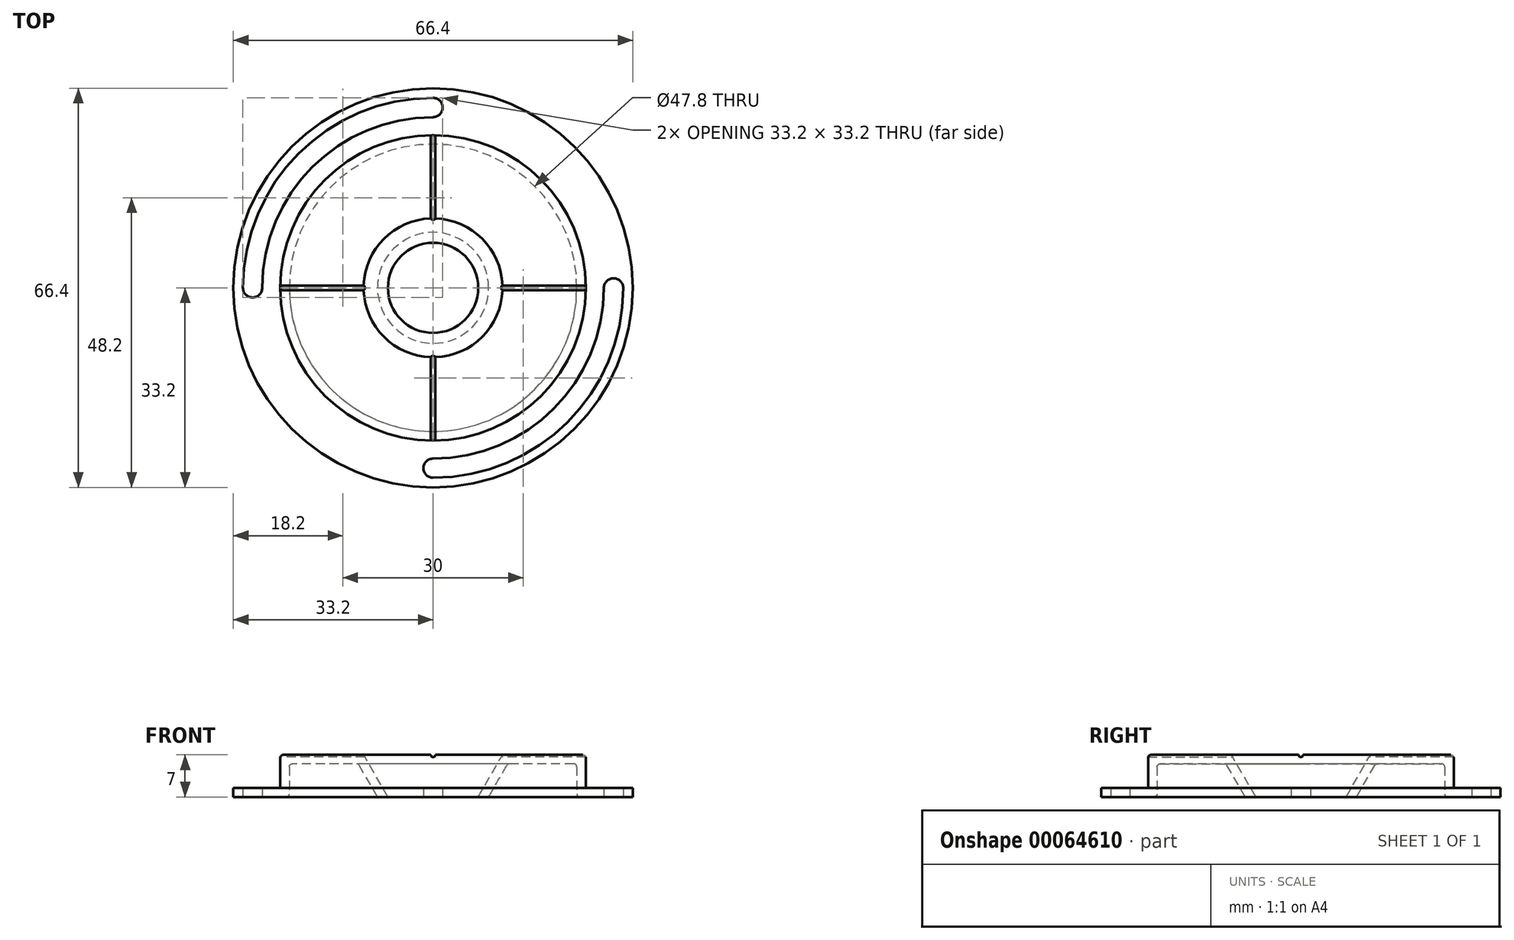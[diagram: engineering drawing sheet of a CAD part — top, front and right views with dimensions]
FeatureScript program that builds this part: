
annotation { "Feature Type Name" : "Feature", "Feature Type Description" : "" }
export const myFeature = defineFeature(function(context is Context, id is Id, definition is map)
    precondition{}
    {
        {
            assignVariable(context, id + "F0", {"name" : "h", "anyValue" : 7});
        }
        {
            assignVariable(context, id + "F1", {"name" : "thickness", "anyValue" : 1.5});
        }
        {
            var Q0;
            Q0=qCreatedBy(makeId("Top.planeOp"),FACE);
            var sketch = newSketch(context, id + "F2", { "sketchPlane" : qUnion([Q0])});
            skLineSegment(sketch, "E0", {"start": v(0, 30) * mm, "end": v(0, -30) * mm, "construction": true});
            skLineSegment(sketch, "E1", {"start": v(-30, 0) * mm, "end": v(30, 0) * mm, "construction": true});
            skLineSegment(sketch, "E2", {"start": v(-21.21, -21.21) * mm, "end": v(21.21, 21.21) * mm, "construction": true});
            skArc(sketch, "E3", {"start": v(-30, 0) * mm, "mid": v(-21.21, -21.21) * mm, "end": v(0, -30) * mm, "construction": true});
            skArc(sketch, "E4", {"start": v(0, -30) * mm, "mid": v(30, 0) * mm, "end": v(0, 30) * mm, "construction": true});
            skArc(sketch, "E5", {"start": v(0, 30) * mm, "mid": v(-21.21, 21.21) * mm, "end": v(-30, 0) * mm, "construction": true});
            skArc(sketch, "E6.0", {"start": v(-22.34, 22.34) * mm, "mid": v(-29.2, 12.1) * mm, "end": v(-31.6, 0) * mm});
            skArc(sketch, "E7.0", {"start": v(-20.08, 20.08) * mm, "mid": v(-26.24, 10.87) * mm, "end": v(-28.4, 0) * mm});
            skArc(sketch, "E8", {"start": v(-31.6, 0) * mm, "mid": v(-30, -1.6) * mm, "end": v(-28.4, 0) * mm});
            skLineSegment(sketch, "E9", {"start": v(0, 0) * mm, "end": v(-21.21, 21.21) * mm, "construction": true});
            skArc(sketch, "E10.MirrorCS", {"start": v(-20.08, 20.08) * mm, "mid": v(-10.87, 26.24) * mm, "end": v(0, 28.4) * mm});
            skArc(sketch, "E11.MirrorCS", {"start": v(-22.34, 22.34) * mm, "mid": v(-12.1, 29.2) * mm, "end": v(0, 31.6) * mm});
            skArc(sketch, "E12.MirrorCS", {"start": v(0, 31.6) * mm, "mid": v(1.6, 30) * mm, "end": v(0, 28.4) * mm});
            skArc(sketch, "E13.MirrorCS", {"start": v(31.6, 0) * mm, "mid": v(30, 1.6) * mm, "end": v(28.4, 0) * mm});
            skArc(sketch, "E14.MirrorCS", {"start": v(22.34, -22.34) * mm, "mid": v(29.2, -12.1) * mm, "end": v(31.6, 0) * mm});
            skArc(sketch, "E15.MirrorCS", {"start": v(20.08, -20.08) * mm, "mid": v(26.24, -10.87) * mm, "end": v(28.4, 0) * mm});
            skArc(sketch, "E16.MirrorCS", {"start": v(20.08, -20.08) * mm, "mid": v(10.87, -26.24) * mm, "end": v(0, -28.4) * mm});
            skArc(sketch, "E17.MirrorCS", {"start": v(22.34, -22.34) * mm, "mid": v(12.1, -29.2) * mm, "end": v(0, -31.6) * mm});
            skArc(sketch, "E18.MirrorCS", {"start": v(0, -31.6) * mm, "mid": v(-1.6, -30) * mm, "end": v(0, -28.4) * mm});
            skCircle(sketch, "E19", {"center": v(0, 0) * mm, "radius": 7.5 * mm});
            skPoint(sketch, "E20", {"position": v(7.5, 0) * mm});
            skSolve(sketch);
        }
        {
            var Q0;
            Q0=qCreatedBy(makeId("Front.planeOp"),FACE);
            var sketch = newSketch(context, id + "F3", { "sketchPlane" : qUnion([Q0])});
            skLineSegment(sketch, "E21", {"start": v(7.5, 0) * mm, "end": v(11.54, 7) * mm});
            skLineSegment(sketch, "E22", {"start": v(11.54, 7) * mm, "end": v(0, 7) * mm});
            skLineSegment(sketch, "E23", {"start": v(0, 7) * mm, "end": v(0, 0) * mm});
            skLineSegment(sketch, "E24", {"start": v(0, 0) * mm, "end": v(7.5, 0) * mm});
            skLineSegment(sketch, "E25", {"start": v(7.5, 0) * mm, "end": v(7.5, 7) * mm, "construction": true});
            skSolve(sketch);
        }
        {
            var Q0;
            Q0=sQuery(id+"F3.wireOp",EDGE,"E23");
            var Q1;
            Q1=sQuery(id+"F3.wireOp",VERTEX,"E23.start");
            cPlane(context, id + "F4", {"entities" : qUnion([Q0, Q1]), "cplaneType" : CPlaneType.LINE_POINT, "offset" : 25 * mm, "width" : 150 * mm, "height" : 150 * mm});
        }
        {
            var Q0;
            Q0=qCreatedBy(id+"F4.planeOp",FACE);
            var sketch = newSketch(context, id + "F5", { "sketchPlane" : qUnion([Q0])});
            skCircle(sketch, "E26", {"center": v(0, 0) * mm, "radius": 25.4 * mm});
            skCircle(sketch, "E27", {"center": v(0, 0) * mm, "radius": 33.2 * mm});
            skSolve(sketch);
        }
        {
            var Q0;
            Q0=makeQuery(id+"F5.imprint","IMPRINT",FACE,{"disambiguationData":[TD([[makeQuery(id+"F5.imprint","IMPRINT",EDGE,{"derivedFrom":sQuery(id+"F5.wireOp",EDGE,"E26")}),-1.0]])]});
            extrude(context, id + "F6", {"entities" : qUnion([Q0]), "depth" : (getVariable(context, 'h')) * mm, "hasSecondDirection" : true, "secondDirectionOppositeDirection" : false, "secondDirectionDepth" : (getVariable(context, 'h') - getVariable(context, 'thickness')) * mm});
        }
        {
            var Q0;
            Q0=makeQuery(id+"F5.imprint","IMPRINT",FACE,{"disambiguationData":[TD([[makeQuery(id+"F5.imprint","IMPRINT",EDGE,{"derivedFrom":sQuery(id+"F5.wireOp",EDGE,"E26")}),1.0]])]});
            var Q1;
            Q1=makeQuery(id+"F6.opExtrude","CAP_FACE",FACE,{"disambiguationData":[OSD([sQuery(id+"F5.wireOp",EDGE,"E26"),sQuery(id+"F5.wireOp",EDGE,"E27")])],"isStart":false});
            extrude(context, id + "F7", {"entities" : qUnion([Q0]), "operationType" : NewBodyOperationType.ADD, "endBound" : BoundingType.UP_TO_SURFACE, "endBoundEntityFace" : qUnion([Q1]), "depth" : 25 * mm});
        }
        {
            var Q0;
            Q0=makeQuery(id+"F3.imprint","IMPRINT",FACE,{"disambiguationData":[TD([[makeQuery(id+"F3.imprint","IMPRINT",EDGE,{"derivedFrom":sQuery(id+"F3.wireOp",EDGE,"E21")}),1.0]])]});
            var Q1;
            Q1=sQuery(id+"F2.wireOp",EDGE,"E19");
            revolve(context, id + "F8", {"entities" : qUnion([Q0]), "axis" : qUnion([Q1]), "revolveType" : RevolveType.FULL, "oppositeDirection" : true});
        }
        {
            var Q0;
            Q0 = qSketchRegion(id + "F2", true);
            extrude(context, id + "F9", {"entities" : qUnion([Q0]), "operationType" : NewBodyOperationType.REMOVE, "endBound" : BoundingType.THROUGH_ALL, "depth" : 25 * mm});
        }
        {
            var Q0;
            Q0=qCreatedBy(makeId("Top.planeOp"),FACE);
            var sketch = newSketch(context, id + "F10", { "sketchPlane" : qUnion([Q0])});
            skCircle(sketch, "E28.0", {"center": v(0, 0) * mm, "radius": 23.9 * mm});
            skSolve(sketch);
        }
        {
            var Q0;
            Q0 = qSketchRegion(id + "F10", true);
            extrude(context, id + "F11", {"entities" : qUnion([Q0]), "depth" : (getVariable(context, 'h') - getVariable(context, 'thickness')) * mm});
        }
        {
            var Q0;
            Q0=makeQuery(id+"F8.opRevolve","SWEPT_BODY",BODY,{"disambiguationData":[OSD([sQuery(id+"F3.wireOp",EDGE,"E21"),sQuery(id+"F3.wireOp",EDGE,"E22"),sQuery(id+"F3.wireOp",EDGE,"E23"),sQuery(id+"F3.wireOp",EDGE,"E24")])]});
            var Q1;
            Q1=makeQuery(id+"F11.opExtrude","SWEPT_BODY",BODY,{"disambiguationData":[OSD([sQuery(id+"F10.wireOp",EDGE,"E28.0")])]});
            var Q2;
            Q2=makeQuery(id+"F8.opRevolve","SWEPT_FACE",FACE,{"disambiguationData":[OSD([sQuery(id+"F3.wireOp",EDGE,"E21")])]});
            booleanBodies(context, id + "F12", {"operationType" : BooleanOperationType.SUBTRACTION, "tools" : qUnion([Q0]), "targets" : qUnion([Q1]), "offset" : true, "entitiesToOffset" : qUnion([Q2]), "offsetDistance" : (getVariable(context, 'thickness')) * mm, "keepTools" : true});
        }
        {
            var Q0;
            Q0=makeQuery(id+"F8.opRevolve","SWEPT_BODY",BODY,{"disambiguationData":[OSD([sQuery(id+"F3.wireOp",EDGE,"E21"),sQuery(id+"F3.wireOp",EDGE,"E22"),sQuery(id+"F3.wireOp",EDGE,"E23"),sQuery(id+"F3.wireOp",EDGE,"E24")])]});
            var Q1;
            Q1=makeQuery(id+"F11.opExtrude","SWEPT_BODY",BODY,{"disambiguationData":[OSD([sQuery(id+"F10.wireOp",EDGE,"E28.0")])]});
            var Q2;
            Q2=makeQuery(id+"F6.opExtrude","SWEPT_BODY",BODY,{"disambiguationData":[OSD([sQuery(id+"F5.wireOp",EDGE,"E26"),sQuery(id+"F5.wireOp",EDGE,"E27")])]});
            booleanBodies(context, id + "F13", {"operationType" : BooleanOperationType.SUBTRACTION, "tools" : qUnion([Q0, Q1]), "targets" : qUnion([Q2])});
        }
        {
            var Q0;
            Q0=makeQuery(id+"F6.opExtrude","CAP_EDGE",EDGE,{"disambiguationData":[OSD([sQuery(id+"F5.wireOp",EDGE,"E26")])],"isStart":true});
            var Q1;
            Q1=makeQuery(id+"F7.opExtrude","CAP_EDGE",EDGE,{"disambiguationData":[OSD([sQuery(id+"F5.wireOp",EDGE,"E26")])],"isStart":true});
            var Q2;
            Q2=makeQuery(id+"F8.boolean.opBoolean","COPY",EDGE,{"derivedFrom":makeQuery(id+"F8.opRevolve","SWEPT_EDGE",EDGE,{"disambiguationData":[OSD([sQuery(id+"F3.wireOp",EDGE,"E21"),sQuery(id+"F3.wireOp",EDGE,"E22")])]})});
            var Q3;
            Q3=makeQuery(id+"F13.opBoolean","COPY",EDGE,{"derivedFrom":makeQuery(id+"F8.opRevolve","SWEPT_EDGE",EDGE,{"disambiguationData":[OSD([sQuery(id+"F3.wireOp",EDGE,"E21"),sQuery(id+"F3.wireOp",EDGE,"E22")])]})});
            var Q4;
            Q4=makeQuery(id+"F13.opBoolean","COPY",EDGE,{"derivedFrom":makeQuery(id+"F11.opExtrude","CAP_EDGE",EDGE,{"disambiguationData":[OSD([sQuery(id+"F10.wireOp",EDGE,"E28.0")])],"isStart":true})});
            var Q5;
            Q5=makeQuery(id+"F13.opBoolean","COPY",EDGE,{"derivedFrom":makeQuery(id+"F11.opExtrude","CAP_EDGE",EDGE,{"disambiguationData":[OSD([sQuery(id+"F10.wireOp",EDGE,"E28.0")])],"isStart":false})});
            var Q6;
            Q6=makeQuery(id+"F13.opBoolean","COPY",EDGE,{"derivedFrom":makeQuery(id+"F12.tempBoolean.opBoolean","INTERSECT",EDGE,{"derivedFrom":[makeQuery(id+"F11.opExtrude","CAP_FACE",FACE,{"disambiguationData":[OSD([sQuery(id+"F10.wireOp",EDGE,"E28.0")])],"isStart":false}),makeQuery(id+"F12.offsetTempBody.opPattern","COPY",FACE,{"derivedFrom":makeQuery(id+"F8.opRevolve","SWEPT_FACE",FACE,{"disambiguationData":[OSD([sQuery(id+"F3.wireOp",EDGE,"E21")])]}),"instanceName":"1"})]})});
            fillet(context, id + "F14", {"entities" : qUnion([Q0, Q1, Q2, Q3, Q4, Q5, Q6]), "radius" : .5 * mm, "tangentPropagation" : true, "allowEdgeOverflow" : false});
        }
        {
            var Q0;
            Q0=qCreatedBy(id+"F4.planeOp",FACE);
            var sketch = newSketch(context, id + "F15", { "sketchPlane" : qUnion([Q0])});
            skCircle(sketch, "E29", {"center": v(0, 0) * mm, "radius": 11.54 * mm, "construction": true});
            skCircle(sketch, "E30.0", {"center": v(0, 0) * mm, "radius": 25.4 * mm, "construction": true});
            skLineSegment(sketch, "E31", {"start": v(0, 0) * mm, "end": v(0, -33.2) * mm});
            skLineSegment(sketch, "E32", {"start": v(0.37, -25.4) * mm, "end": v(0.37, 0) * mm});
            skLineSegment(sketch, "E33", {"start": v(0.37, 0) * mm, "end": v(0, 0) * mm});
            skLineSegment(sketch, "E34", {"start": v(0, -25.4) * mm, "end": v(0.37, -25.4) * mm});
            skSolve(sketch);
        }
        {
            var Q0;
            Q0 = qSketchRegion(id + "F15", true);
            var Q1;
            Q1=sQuery(id+"F15.wireOp",EDGE,"E31");
            revolve(context, id + "F16", {"entities" : qUnion([Q0]), "axis" : qUnion([Q1]), "revolveType" : RevolveType.FULL});
        }
        {
            var Q0;
            Q0=makeQuery(id+"F16.opRevolve","SWEPT_BODY",BODY,{"disambiguationData":[OSD([sQuery(id+"F15.wireOp",EDGE,"E31"),sQuery(id+"F15.wireOp",EDGE,"E32"),sQuery(id+"F15.wireOp",EDGE,"E33"),sQuery(id+"F15.wireOp",EDGE,"E34")])]});
            var Q1;
            Q1=sQuery(id+"F3.wireOp",EDGE,"E23");
            circularPattern(context, id + "F17", {"operationType" : NewBodyOperationType.REMOVE, "entities" : qUnion([Q0]), "axis" : qUnion([Q1]), "angle" : 360 * degree, "instanceCount" : 4, "equalSpace" : true});
        }
    });
